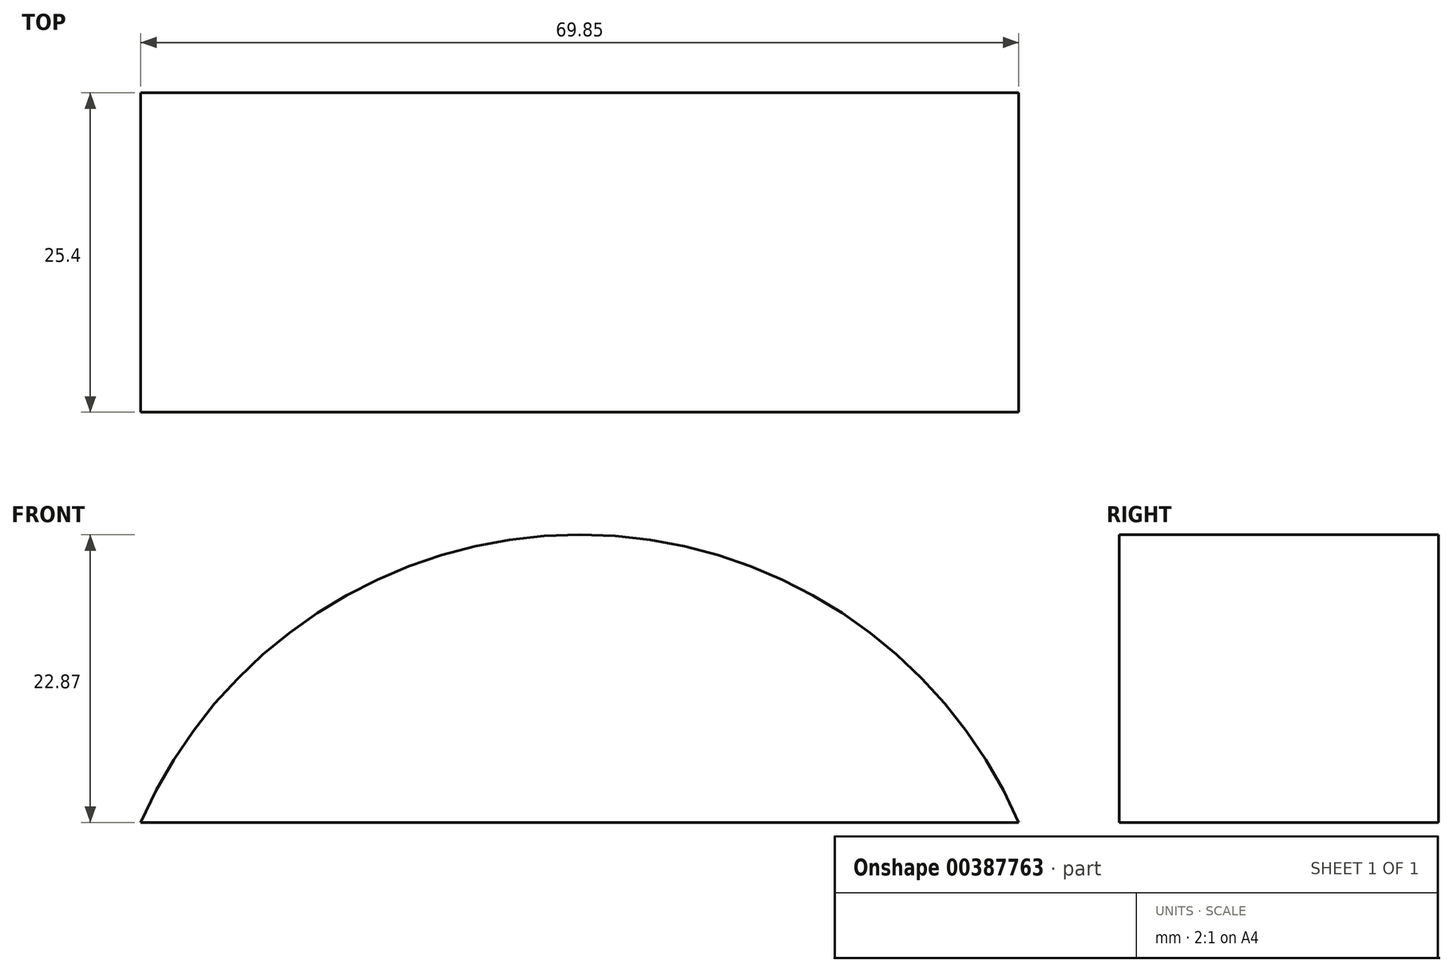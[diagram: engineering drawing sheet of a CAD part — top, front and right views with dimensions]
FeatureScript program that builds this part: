
annotation { "Feature Type Name" : "Feature", "Feature Type Description" : "" }
export const myFeature = defineFeature(function(context is Context, id is Id, definition is map)
    precondition{}
    {
        {
            var Q0;
            Q0=qCreatedBy(makeId("Front.planeOp"),FACE);
            var sketch = newSketch(context, id + "F0", { "sketchPlane" : qUnion([Q0])});
            skLineSegment(sketch, "E0", {"start": v(0, 0) * mm, "end": v(69.85, 0) * mm});
            skArc(sketch, "E1", {"start": v(69.85, 0) * mm, "mid": v(34.93, 22.87) * mm, "end": v(0, 0) * mm});
            skSolve(sketch);
        }
        {
            var Q0;
            Q0 = qSketchRegion(id + "F0", true);
            extrude(context, id + "F1", {"entities" : qUnion([Q0]), "depth" : 25.4 * mm});
        }
    });
